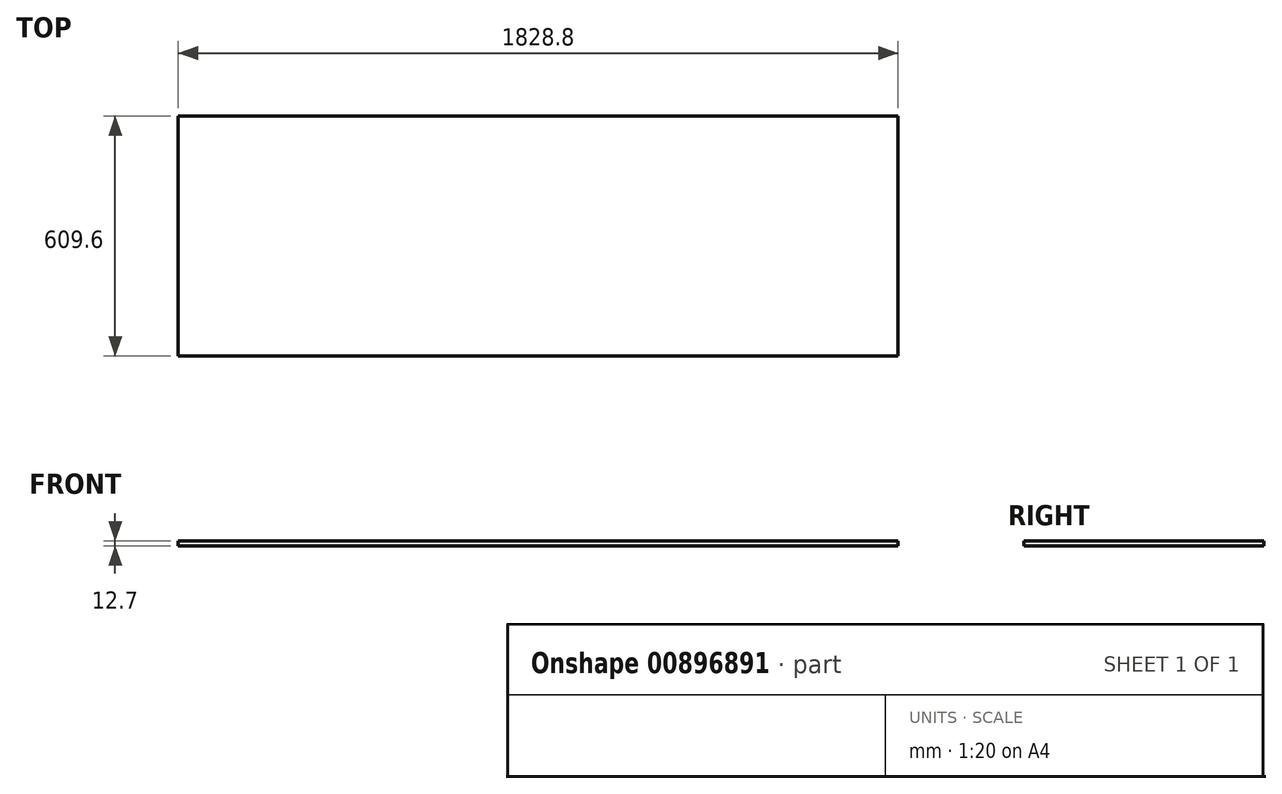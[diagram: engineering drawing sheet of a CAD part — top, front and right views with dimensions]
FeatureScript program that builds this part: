
annotation { "Feature Type Name" : "Feature", "Feature Type Description" : "" }
export const myFeature = defineFeature(function(context is Context, id is Id, definition is map)
    precondition{}
    {
        {
            var Q0;
            Q0=qCreatedBy(makeId("Top.planeOp"),FACE);
            var sketch = newSketch(context, id + "F0", { "sketchPlane" : qUnion([Q0])});
            skLineSegment(sketch, "E0.bottom", {"start": v(-914.4, 304.8) * mm, "end": v(914.4, 304.8) * mm});
            skLineSegment(sketch, "E0.top", {"start": v(-914.4, -304.8) * mm, "end": v(914.4, -304.8) * mm});
            skLineSegment(sketch, "E0.left", {"start": v(-914.4, 304.8) * mm, "end": v(-914.4, -304.8) * mm});
            skLineSegment(sketch, "E0.right", {"start": v(914.4, 304.8) * mm, "end": v(914.4, -304.8) * mm});
            skPoint(sketch, "E0.middle", {"position": v(0, 0) * mm});
            skSolve(sketch);
        }
        {
            var Q0;
            Q0 = qSketchRegion(id + "F0", true);
            extrude(context, id + "F1", {"entities" : qUnion([Q0]), "oppositeDirection" : true, "depth" : 12.7 * mm, "offsetDistance" : 25.4 * mm});
        }
    });
